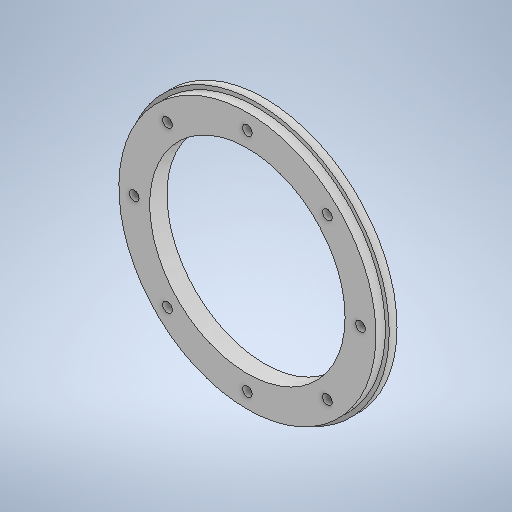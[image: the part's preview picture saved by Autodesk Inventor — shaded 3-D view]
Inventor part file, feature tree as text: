
AUTODESK INVENTOR PART (.ipt)
format: ipt  version: 2025 (Build 290162010, 162A)  size: 381,440 bytes
history: native  units: mm
features: extrude x5, sketch x5, projected_geometry x3, other x2, pattern_circular x1
ambient origin geometry x8: Origin, YZ Plane, XZ Plane, XY Plane, X Axis, Y Axis, Z Axis, Center Point
bodies: Solid1 (feature_tree)
feature tree (16):
  extrude  "Extrusion1"  Depth=250.0mm
  extrude  "Extrusion2"  Depth=12.5mm
  extrude  "Extrusion3"  Depth=80.0mm TaperAngle=360.0deg
  pattern_circular  "Circular Pattern1"  [2 undecoded]
  extrude  "Extrusion4"  Depth=10.0mm TaperAngle=0.0deg
  extrude  "Extrusion5"  Depth=10.0mm
  other  "A-Side Definition"
  sketch  "Sketch1"  dims[d0=39.5mm d1=250.0mm]
  sketch  "Sketch2"  dims[d2=41.0mm d3=0.0mm d4=12.5mm]
  projected_geometry  "Projected Loop1"
  sketch  "Sketch3"  dims[d5=0.0mm d6=0.0mm d7=80.0mm d8=360.0deg]
  sketch  "Sketch4"  dims[d10=27.5mm]
  sketch  "Sketch5"  dims[d11=11.0mm d12=0.0mm d13=5.0mm d14=10.0mm d15=0.0mm d16=19.0mm d17=41.0mm d18=0.0mm d19=0.0mm]
  projected_geometry  "Projected Loop2"
  projected_geometry  "Projected Loop3"
  other  "Definition1"
note: 2 required parameter values undecoded (feature->parameter linkage not recoverable at this tier; creation-order binding heuristic only, values carry confidence <= 0.55)
